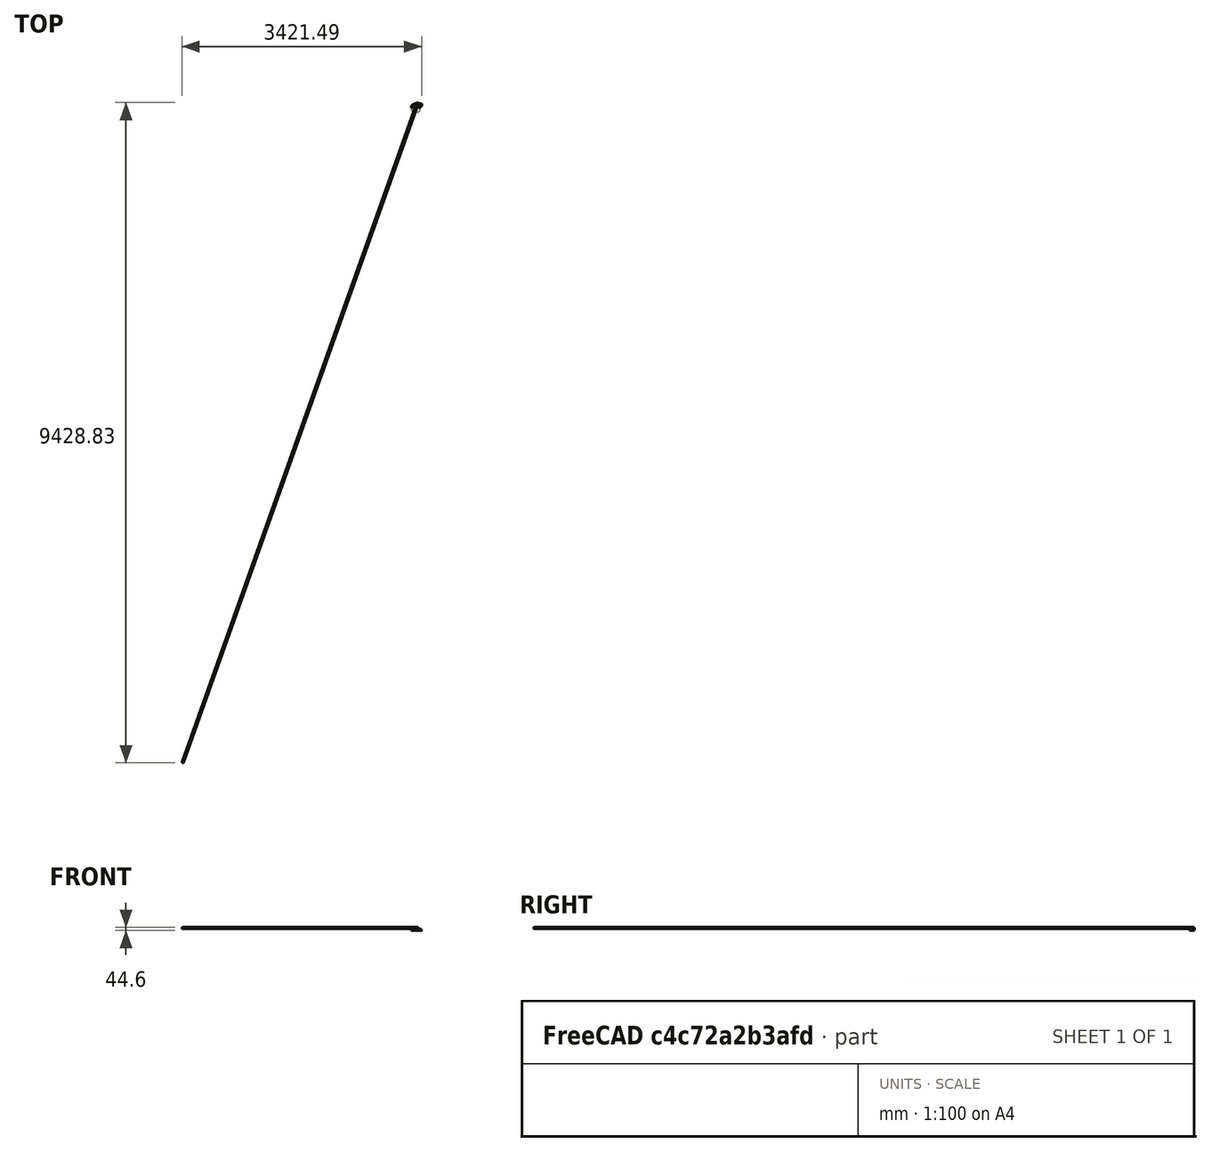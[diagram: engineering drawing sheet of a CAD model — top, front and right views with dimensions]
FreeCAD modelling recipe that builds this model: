
FCSTD DOCUMENT  (FreeCAD 0.16R)
Label: V1
License: All rights reserved
LicenseURL: http://en.wikipedia.org/wiki/All_rights_reserved
objects: Sketcher::SketchObject×6, PartDesign::Pad×4, PartDesign::Fillet×2, PartDesign::Pocket×1, Mesh::Feature×1
note: 18 computed .brp shape members not serialized (recipe doc carries the construction recipe); baked Part::Feature solids carry a one-line shape summary decoded from their .brp

FEATURE [Sketcher::SketchObject] Sketch
  sketch-geometry (11):
    g0: ArcOfCircle CenterX=0 CenterY=0 CenterZ=0 NormalX=0 NormalY=0 NormalZ=1 Radius=65 StartAngle=1.5708 EndAngle=2.86744
    g1: ArcOfCircle CenterX=0 CenterY=0 CenterZ=0 NormalX=0 NormalY=0 NormalZ=1 Radius=48 StartAngle=0.377003 EndAngle=2.75854
    g2: LineSegment StartX=2.40667e-07 StartY=65 StartZ=0 EndX=79.4942 EndY=65 EndZ=0
    g3: LineSegment StartX=47.168 StartY=15.3736 StartZ=0 EndX=54.9232 EndY=15.3842 EndZ=0
    g4: LineSegment StartX=84.8824 StartY=59.6118 StartZ=0 EndX=84.8824 EndY=45.3841 EndZ=0
    g5: ArcOfCircle CenterX=54.8824 CenterY=45.3841 CenterZ=0 NormalX=0 NormalY=0 NormalZ=1 Radius=30 StartAngle=4.71375 EndAngle=6.28319
    g6: ArcOfCircle CenterX=79.4942 CenterY=59.6118 CenterZ=0 NormalX=0 NormalY=0 NormalZ=1 Radius=5.38817 StartAngle=0 EndAngle=1.5708
    g7: ArcOfCircle CenterX=49.0502 CenterY=20.0058 CenterZ=0 NormalX=0 NormalY=0 NormalZ=1 Radius=5 StartAngle=3.62755 EndAngle=4.32643
    g8: ArcOfCircle CenterX=-60.5912 CenterY=17.3257 CenterZ=0 NormalX=0 NormalY=0 NormalZ=1 Radius=2 StartAngle=3.00536 EndAngle=4.40537
    g9: ArcOfCircle CenterX=-48.9002 CenterY=20.3538 CenterZ=0 NormalX=0 NormalY=0 NormalZ=1 Radius=5 StartAngle=4.8743 EndAngle=5.77943
    g10: LineSegment StartX=-61.1956 StartY=15.4192 StartZ=0 EndX=-48.0942 EndY=15.4192 EndZ=0
  constraints (35):
    c: Radius(g0) = 65
    c: Coincident(g-1,g0)
    c: PointOnObject(g1,g-2)
    c: Coincident(g1,g-1)
    c: Radius(g1) = 48
    c: Horizontal(g2)
    c: Coincident(g0,g2)
    c: Vertical(g4)
    c: Tangent(g4,g5) = 1.5708
    c: Tangent(g3,g5) = -1.5708
    c: Tangent(g4,g6) = 1.5708
    c: Tangent(g2,g6) = 1.5708
    c: Radius(g7) = 5
    c: Radius(g9) = 5
    c: Radius(g8) = 2
    c: Coincident(g3,g7)
    c: Coincident(g1,g7)
    c: Coincident(g10,g9)
    c: Coincident(g1,g9)
    c: Coincident(g10,g8)
    c: Coincident(g0,g8)
    c: Distance(g10) = 13.1014
    c: Distance(g2) = 79.4942
    c: Distance(g3) = 7.75526
    c: Distance(g4) = 14.2277
    c: Radius(g5) = 30
    c: Radius(g6) = 5.38817
    c: DistanceY(g-1,g2) = 65
    c: DistanceY(g3) = 15.3736
    c: DistanceY(g9) = 15.4192
    c: DistanceY(g0) = 17.5973
    c: DistanceY(g1) = 17.9402
    c: DistanceY(g8) = 15.4192
    c: DistanceY(g1) = 17.6705
    c: DistanceX(g8) = -61.1956
FEATURE [Sketcher::SketchObject] Sketch002
  Placement = pos=(0,0,1) rot=(0,0,1;0rad)
  sketch-geometry (8):
    g0: ArcOfCircle CenterX=0 CenterY=0 CenterZ=0 NormalX=0 NormalY=0 NormalZ=1 Radius=48 StartAngle=0.377003 EndAngle=2.75854
    g1: LineSegment StartX=47.0328 StartY=15.3736 StartZ=0 EndX=54.7867 EndY=15.2303 EndZ=0
    g2: ArcOfCircle CenterX=55.341 CenterY=45.2252 CenterZ=0 NormalX=0 NormalY=0 NormalZ=1 Radius=30 StartAngle=4.69391 EndAngle=6.10812
    g3: ArcOfCircle CenterX=49.0887 CenterY=19.9313 CenterZ=0 NormalX=0 NormalY=0 NormalZ=1 Radius=5 StartAngle=3.61079 EndAngle=4.28863
    g4: ArcOfCircle CenterX=-48.9021 CenterY=20.3504 CenterZ=0 NormalX=0 NormalY=0 NormalZ=1 Radius=5 StartAngle=4.91142 EndAngle=5.7802
    g5: ArcOfCircle CenterX=-0.655187 CenterY=1.27485 CenterZ=0 NormalX=0 NormalY=0 NormalZ=1 Radius=51 StartAngle=0.862262 EndAngle=2.75615
    g6: LineSegment StartX=84.8825 StartY=40 StartZ=0 EndX=32.5316 EndY=40 EndZ=0
    g7: LineSegment StartX=-47.9135 StartY=20.4491 StartZ=0 EndX=-47.9135 EndY=15.4491 EndZ=0
  constraints (29):
    c: PointOnObject(g0,g-2)
    c: Coincident(g0,g-1)
    c: Radius(g0) = 48
    c: Tangent(g1,g2) = -1.5708
    c: Radius(g3) = 5
    c: Radius(g4) = 5
    c: Coincident(g1,g3)
    c: Coincident(g0,g3)
    c: Coincident(g0,g4)
    c: Distance(g1) = 7.75526
    c: Radius(g2) = 30
    c: DistanceY(g1) = 15.3736
    c: DistanceY(g0) = 17.9402
    c: DistanceY(g0) = 17.6705
    c: DistanceX(g4,g5) = 0
    c: DistanceX(g5) = -47.9135
    c: DistanceY(g4) = 15.4491
    c: DistanceY(g4,g5) = 5
    c: Radius(g5) = 51
    c: Coincident(g6,g2)
    c: Coincident(g5,g6)
    c: Vertical(g7)
    c: Coincident(g7,g5)
    c: Coincident(g7,g4)
    c: DistanceY(g5) = 40
    c: DistanceX(g2) = 84.8825
    c: DistanceY(g1) = 15.2303
    c: DistanceX(g5) = 32.5316
    c: Horizontal(g6)
FEATURE [PartDesign::Pad] Pad002  label="Stiffener"
  Length = 1
  Length2 = 100
  Placement = pos=(0,0,1) rot=(0,0,1;0rad)
  Sketch = -> Sketch002
  Type = 0
FEATURE [PartDesign::Pad] Pad  label="Faceplate"
  Length = 1
  Length2 = 100
  Sketch = -> Sketch
  Type = 0
FEATURE [Sketcher::SketchObject] Sketch001
  Placement = pos=(0,0,1) rot=(0,0,1;0rad)
  Support = -> Pad [Face13]
  sketch-geometry (6):
    g0: ArcOfCircle CenterX=0 CenterY=0 CenterZ=0 NormalX=0 NormalY=0 NormalZ=1 Radius=65 StartAngle=1.5708 EndAngle=2.88461
    g1: LineSegment StartX=6.04881e-05 StartY=65 StartZ=0 EndX=80.0001 EndY=65 EndZ=0
    g2: LineSegment StartX=80.0001 StartY=63 StartZ=0 EndX=6.04881e-05 EndY=63 EndZ=0
    g3: LineSegment StartX=80.0001 StartY=65 StartZ=0 EndX=80.0001 EndY=63 EndZ=0
    g4: ArcOfCircle CenterX=0.26057 CenterY=1.00055 CenterZ=0 NormalX=0 NormalY=0 NormalZ=1 Radius=62 StartAngle=1.575 EndAngle=2.88858
    g5: LineSegment StartX=-62.8655 StartY=16.5204 StartZ=0 EndX=-59.7655 EndY=16.5204 EndZ=0
  constraints (19):
    c: Radius(g0) = 65
    c: Coincident(g-1,g0)
    c: Horizontal(g1)
    c: Coincident(g0,g1)
    c: DistanceY(g-1,g1) = 65
    c: Horizontal(g2)
    c: Equal(g2,g1)
    c: DistanceX(g0,g2) = 0
    c: Coincident(g3,g2)
    c: Coincident(g3,g1)
    c: DistanceY(g2,g1) = 2
    c: Radius(g4) = 62
    c: Coincident(g4,g2)
    c: DistanceX(g0,g4) = 3.1
    c: DistanceY(g4,g0) = 0
    c: DistanceY(g-1,g0) = 16.5204
    c: Coincident(g4,g5)
    c: Coincident(g5,g0)
    c: Distance(g1) = 80
FEATURE [PartDesign::Pad] Pad004  label="Connector"
  Length = 20
  Length2 = 100
  Sketch = -> Sketch001
  Type = 0
FEATURE [PartDesign::Fillet] Fillet
  Base = -> Pad004 [Edge52]
  Radius = 10
FEATURE [PartDesign::Fillet] Fillet001
  Base = -> Fillet [Edge25]
  Radius = 2
FEATURE [Sketcher::SketchObject] Sketch003
  Placement = pos=(0,0,1) rot=(0,0,1;0rad)
  Support = -> Fillet001 [Face14]
FEATURE [Sketcher::SketchObject] Sketch004
  ExternalGeometry = -> [Fillet001]
  Placement = pos=(0,0,1) rot=(0,0,1;0rad)
  Support = -> Fillet001 [Face14]
  sketch-geometry (5):
    g0: LineSegment [constr] StartX=0 StartY=0 StartZ=0 EndX=33.5452 EndY=94.2057 EndZ=0
    g1: LineSegment StartX=12.819 StartY=80.7159 StartZ=0 EndX=41.0808 EndY=70.6523 EndZ=0
    g2: LineSegment StartX=41.0808 StartY=70.6523 StartZ=0 EndX=39.0681 EndY=65 EndZ=0
    g3: LineSegment StartX=39.0681 StartY=65 StartZ=0 EndX=7.22286 EndY=65 EndZ=0
    g4: LineSegment StartX=7.22286 StartY=65 StartZ=0 EndX=12.819 EndY=80.7159 EndZ=0
  constraints (15):
    c: Coincident(g0,g-1)
    c: Coincident(g1,g2)
    c: Coincident(g2,g3)
    c: Coincident(g3,g4)
    c: Coincident(g4,g1)
    c: Perpendicular(g0,g1)
    c: Parallel(g4,g0)
    c: Parallel(g2,g0)
    c: Distance(g1) = 30
    c: Symmetric(g1,g1,g0)
    c: Parallel(g3,g-3)
    c: Distance(g2) = 6
    c: PointOnObject(g3,g-3)
    c: Angle(g0) = 1.22871
    c: Distance(g0) = 100
FEATURE [PartDesign::Pad] Pad005
  Length = 35
  Length2 = 1
  Sketch = -> Sketch004
  Type = 4
FEATURE [Sketcher::SketchObject] Sketch005
  Placement = pos=(26.9499,75.6841,0) rot=(0.121238,0.701891,0.701891;2.90029rad)
  Support = -> Pad005 [Face1]
  sketch-geometry (1):
    g0: Circle CenterX=0 CenterY=35 CenterZ=0 NormalX=0 NormalY=0 NormalZ=1 Radius=9.6
  constraints (3):
    c: PointOnObject(g0,g-2)
    c: Radius(g0) = 9.6
    c: DistanceY(g-1,g0) = 35
FEATURE [PartDesign::Pocket] Pocket
  Length = 5
  Sketch = -> Sketch005
  Type = 1
FEATURE [Mesh::Feature] Mesh  label="Pocket (Meshed)"
